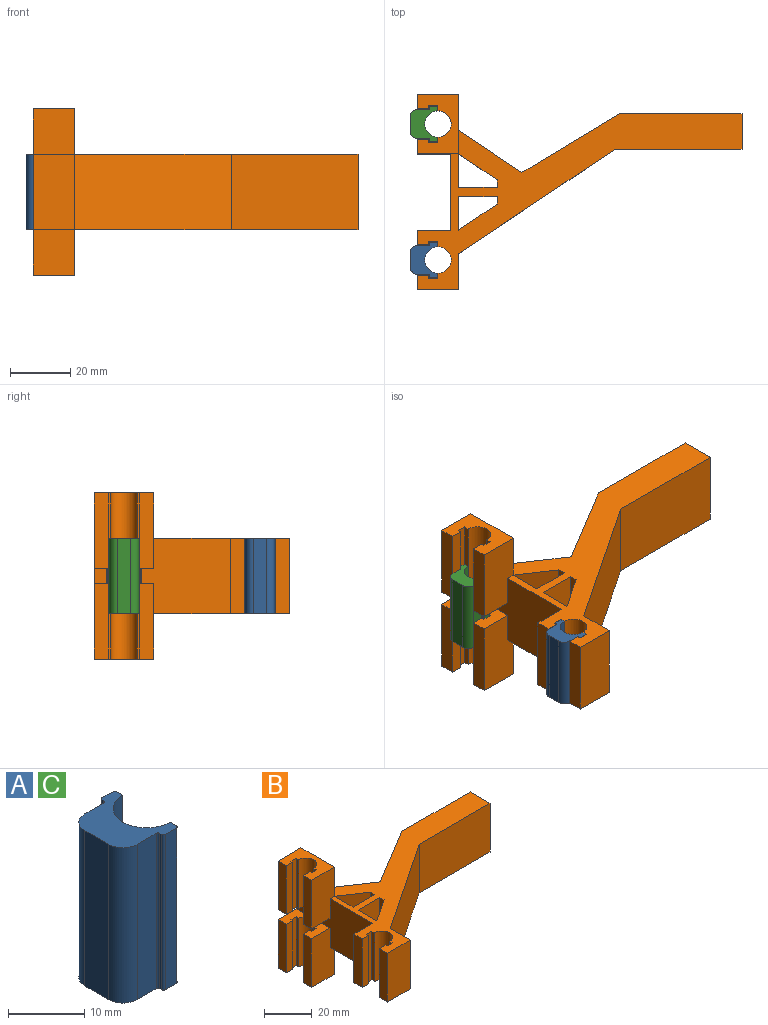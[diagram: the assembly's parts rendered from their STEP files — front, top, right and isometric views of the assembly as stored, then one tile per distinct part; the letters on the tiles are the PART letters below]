
ASSEMBLY  parts=3 mates=2
PART A: 20 faces, bbox 9.3x11.8x25 mm
  f0: plane 25x2.07mm, normal (0,1,0), area 51.9mm2, adj f10,f11,f14,f16
  f1: plane 25x0.32mm, normal (-1,0,0), area 8.1mm2, adj f10,f11,f14,f15
  f2: plane 25x3.51mm, normal (0,1,0), area 87.7mm2, adj f10,f11,f12,f15
  f3: plane 25x4.44mm, normal (-1,0,0), area 111mm2, adj f10,f11,f12,f13
  f4: plane 25x3.51mm, normal (0,-1,0), area 87.7mm2, adj f10,f11,f13,f17
  f5: plane 25x0.32mm, normal (-1,0,0), area 8.1mm2, adj f10,f11,f17,f18
  f6: plane 25x2.07mm, normal (0,-1,0), area 51.9mm2, adj f10,f11,f18,f19
  f7: plane 25x1.16mm, normal (1,0,0), area 29.1mm2, adj f8,f10,f11,f19
  f8: cylinder r=4.38mm len=25mm, axis (0,0,-1), area 343.6mm2, adj f7,f9,f10,f11
  f9: plane 25x1.16mm, normal (1,0,0), area 29.1mm2, adj f8,f10,f11,f16
  f10: plane 11.75x9.25mm, normal (0,0,1), area 62.5mm2, adj f0,f1,f2,f3,f4,f5,f6,f7
  f11: plane 11.75x9.25mm, normal (0,0,-1), area 62.5mm2, adj f0,f1,f2,f3,f4,f5,f6,f7
  f12: cylinder r=2.66mm len=25mm, axis (0,0,-1), area 104.3mm2, adj f2,f3,f10,f11
  f13: cylinder r=2.66mm len=25mm, axis (0,0,1), area 104.3mm2, adj f3,f4,f10,f11
  f14: cylinder r=0.34mm len=25mm, axis (0,0,-1), area 13.3mm2, adj f0,f1,f10,f11
  f15: cylinder r=0.34mm len=25mm, axis (0,0,1), area 13.3mm2, adj f1,f2,f10,f11
  f16: cylinder r=0.34mm len=25mm, axis (0,0,1), area 13.3mm2, adj f0,f9,f10,f11
  f17: cylinder r=0.34mm len=25mm, axis (0,0,1), area 13.3mm2, adj f4,f5,f10,f11
  f18: cylinder r=0.34mm len=25mm, axis (0,0,-1), area 13.3mm2, adj f5,f6,f10,f11
  f19: cylinder r=0.34mm len=25mm, axis (0,0,1), area 13.3mm2, adj f6,f7,f10,f11
PART B: 63 faces, bbox 107.4x64.8x55 mm
  f0: plane 25x4.91mm, normal (-1,0,0), area 122.6mm2, adj f3,f43,f57,f60
  f1: plane 25x4.91mm, normal (-1,0,0), area 122.6mm2, adj f2,f11,f57,f59
  f2: plane 25x13.59mm, normal (0,-1,0), area 314.1mm2, adj f1,f12,f15,f56,f57,f59
  f3: plane 25x3.79mm, normal (0,-1,0), area 94.9mm2, adj f0,f4,f57,f60
  f4: plane 25x1mm, normal (1,0,0), area 25mm2, adj f3,f5,f57,f60
  f5: plane 25x3mm, normal (0,-1,0), area 75mm2, adj f4,f6,f57,f60
  f6: plane 25x1.63mm, normal (-1,0,0), area 40.6mm2, adj f5,f7,f57,f60
  f7: cylinder r=4.38mm len=55mm, axis (0,0,-1), area 698.7mm2, adj f6,f8,f12,f13,f48,f49,f57,f58
  f8: plane 25x1.63mm, normal (-1,0,0), area 40.6mm2, adj f7,f9,f57,f59
  f9: plane 25x3mm, normal (0,1,0), area 75mm2, adj f8,f10,f57,f59
  f10: plane 25x1mm, normal (1,0,0), area 25mm2, adj f9,f11,f57,f59
  f11: plane 25x3.79mm, normal (0,1,0), area 94.9mm2, adj f1,f10,f57,f59
  f12: plane 33.96x25mm, normal (-1,0,0), area 673.6mm2, adj f2,f7,f16,f22,f23,f56,f58,f59
  f13: plane 19.81x13.59mm, normal (0,0,-1), area 165.2mm2, adj f7,f15,f22,f43,f44,f45,f46,f47
  f14: plane 25x11.09mm, normal (1,0,0), area 277.4mm2, adj f16,f20,f53,f56
  f15: plane 55x19.81mm, normal (1,0,0), area 892.1mm2, adj f2,f13,f16,f22,f42,f43,f56,f57
  f16: plane 107.45x58.34mm, normal (0,0,-1), area 1479mm2, adj f12,f14,f15,f17,f18,f19,f20,f21
  f17: plane 25x12.85mm, normal (-0.56,0.83,0), area 386.5mm2, adj f16,f18,f55,f56
  f18: plane 25x11.09mm, normal (1,0,0), area 277.4mm2, adj f16,f17,f19,f56
  f19: plane 25x12.85mm, normal (0,-1,0), area 321.2mm2, adj f16,f18,f55,f56
  f20: plane 25x12.85mm, normal (-0.56,-0.83,0), area 386.5mm2, adj f14,f16,f21,f56
  f21: plane 25x2.5mm, normal (-1,0,0), area 62.5mm2, adj f16,f20,f53,f56
  f22: plane 25x13.59mm, normal (0,-1,0), area 314.1mm2, adj f12,f13,f15,f16,f54,f58
  f23: plane 25x11.02mm, normal (0,1,0), area 275.5mm2, adj f12,f16,f24,f56
  f24: plane 25x4.91mm, normal (-1,0,0), area 122.6mm2, adj f16,f23,f25,f56
  f25: plane 25x3.79mm, normal (0,-1,0), area 94.9mm2, adj f16,f24,f26,f56
  f26: plane 25x1mm, normal (1,0,0), area 25mm2, adj f16,f25,f27,f56
  f27: plane 25x3mm, normal (0,-1,0), area 75mm2, adj f16,f26,f28,f56
  f28: plane 25x1.63mm, normal (-1,0,0), area 40.6mm2, adj f16,f27,f29,f56
  f29: cylinder r=4.38mm len=25mm, axis (0,0,-1), area 343.6mm2, adj f16,f28,f30,f56
  f30: plane 25x1.63mm, normal (-1,0,0), area 40.6mm2, adj f16,f29,f31,f56
  f31: plane 25x3mm, normal (0,1,0), area 75mm2, adj f16,f30,f32,f56
  f32: plane 25x1mm, normal (1,0,0), area 25mm2, adj f16,f31,f33,f56
  f33: plane 25x3.79mm, normal (0,1,0), area 94.9mm2, adj f16,f32,f34,f56
  f34: plane 25x4.91mm, normal (-1,0,0), area 122.6mm2, adj f16,f33,f35,f56
  f35: plane 25x13.59mm, normal (0,-1,0), area 339.7mm2, adj f16,f34,f36,f56
  f36: plane 25x11.91mm, normal (1,0,0), area 297.7mm2, adj f16,f35,f37,f56
  f37: plane 51.89x34.71mm, normal (0.56,-0.83,0), area 1560.7mm2, adj f16,f36,f38,f56
  f38: plane 41.97x25mm, normal (0,-1,0), area 1049.2mm2, adj f16,f37,f39,f56
  f39: plane 25x11.72mm, normal (1,0,0), area 293mm2, adj f16,f38,f40,f56
  f40: plane 40.56x25mm, normal (0,1,0), area 1014mm2, adj f16,f39,f41,f56
  f41: plane 32.28x25mm, normal (-0.52,0.86,0), area 942.6mm2, adj f16,f40,f42,f56
  f42: plane 25x21.02mm, normal (0.56,0.83,0), area 632.3mm2, adj f15,f16,f41,f56
  f43: plane 55x13.59mm, normal (0,1,0), area 692.3mm2, adj f0,f13,f15,f44,f57,f60,f61,f62
  f44: plane 25x4.91mm, normal (-1,0,0), area 122.6mm2, adj f13,f43,f45,f61
  f45: plane 25x3.79mm, normal (0,-1,0), area 94.9mm2, adj f13,f44,f46,f61
  f46: plane 25x1mm, normal (1,0,0), area 25mm2, adj f13,f45,f47,f61
  f47: plane 25x3mm, normal (0,-1,0), area 75mm2, adj f13,f46,f48,f61
  f48: plane 25x1.63mm, normal (-1,0,0), area 40.6mm2, adj f7,f13,f47,f61
  f49: plane 25x1.63mm, normal (-1,0,0), area 40.6mm2, adj f7,f13,f50,f58
  f50: plane 25x3mm, normal (0,1,0), area 75mm2, adj f13,f49,f51,f58
  f51: plane 25x1mm, normal (1,0,0), area 25mm2, adj f13,f50,f52,f58
  f52: plane 25x3.79mm, normal (0,1,0), area 94.9mm2, adj f13,f51,f54,f58
  f53: plane 25x12.85mm, normal (0,1,0), area 321.2mm2, adj f14,f16,f21,f56
  f54: plane 25x4.91mm, normal (-1,0,0), area 122.6mm2, adj f13,f22,f52,f58
  f55: plane 25x2.5mm, normal (-1,0,0), area 62.5mm2, adj f16,f17,f19,f56
  f56: plane 107.45x58.34mm, normal (0,0,1), area 1479mm2, adj f2,f12,f14,f15,f17,f18,f19,f20
  f57: plane 19.81x13.59mm, normal (0,0,1), area 165.2mm2, adj f0,f1,f2,f3,f4,f5,f6,f7
  f58: plane 11.02x8.77mm, normal (0,0,1), area 57.3mm2, adj f7,f12,f22,f49,f50,f51,f52,f54
  f59: plane 11.02x8.77mm, normal (0,0,-1), area 57.3mm2, adj f1,f2,f7,f8,f9,f10,f11,f12
  f60: plane 11.02x8.77mm, normal (0,0,-1), area 57.3mm2, adj f0,f3,f4,f5,f6,f7,f43,f62
  f61: plane 11.02x8.77mm, normal (0,0,1), area 57.3mm2, adj f7,f43,f44,f45,f46,f47,f48,f62
  f62: plane 8.77x5mm, normal (-1,0,0), area 43.9mm2, adj f7,f43,f60,f61
PART C: same geometry as A
PLACE A t=(-5.11,-23.03,0)mm
PLACE B at identity fixed
PLACE C t=(-5.11,21.97,0)mm
MATE slider A.f8 <-> B.f29  axis (0,0,1) through (-2.99,-22.5,25)mm
MATE slider C.f8 <-> B.f7  axis (0,0,1) through (-2.99,22.5,25)mm
